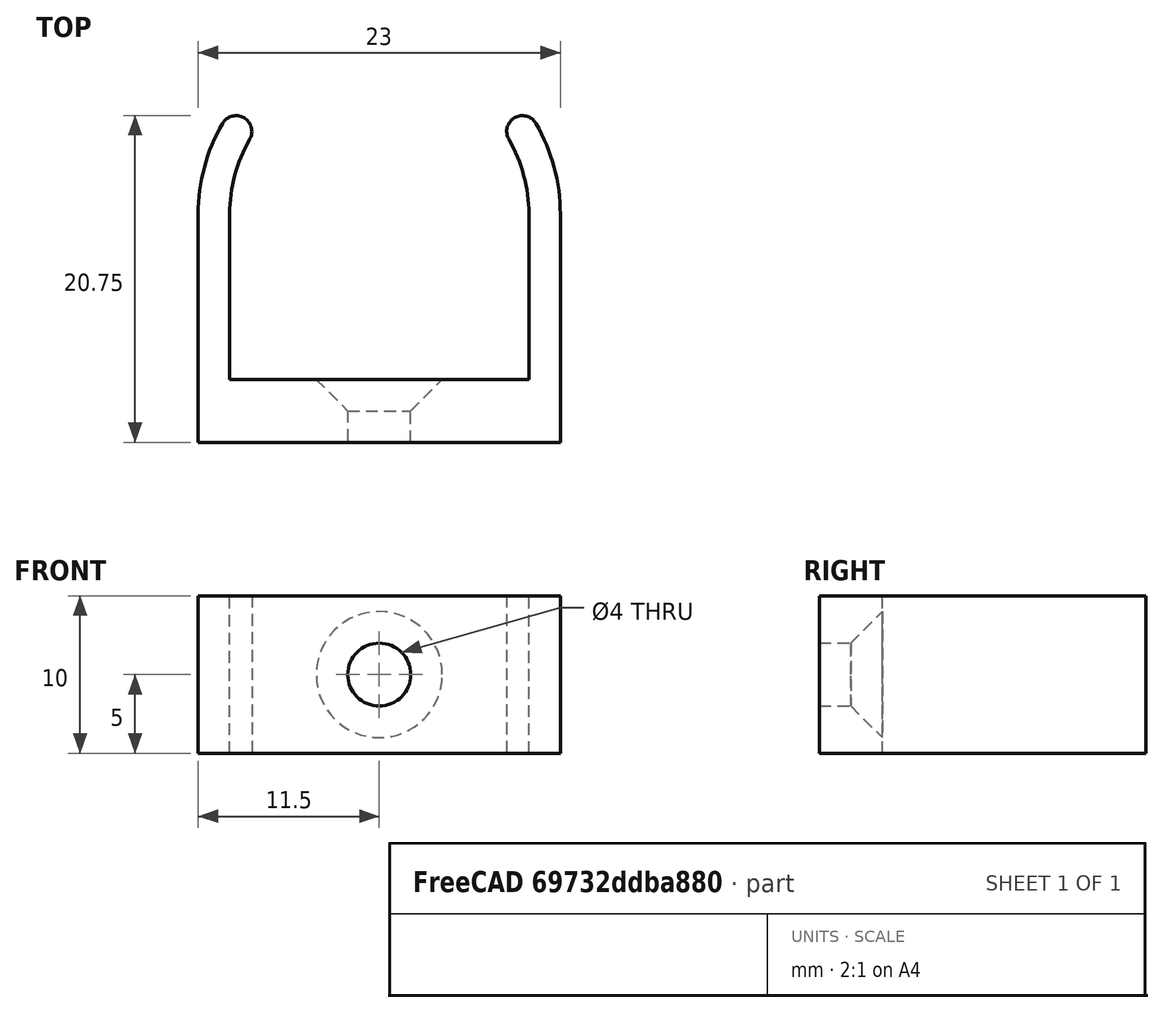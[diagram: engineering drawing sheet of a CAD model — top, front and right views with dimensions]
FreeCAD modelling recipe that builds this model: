
FCSTD DOCUMENT  (FreeCAD 0.20R)
Label: Support_batterie_V1
License: All rights reserved
LicenseURL: http://en.wikipedia.org/wiki/All_rights_reserved
objects: Sketcher::SketchObject×2, PartDesign::Pad×1, PartDesign::Pocket×1, PartDesign::Chamfer×1, PartDesign::Body×1, Mesh::Feature×1
note: 9 computed .brp shape members not serialized (recipe doc carries the construction recipe); baked Part::Feature solids carry a one-line shape summary decoded from their .brp

FEATURE [Sketcher::SketchObject] Sketch
  FullyConstrained = true
  MapMode = 5
  Support = -> [XY_Plane]
  sketch-geometry (15):
    g0: Circle CenterX=0 CenterY=0 CenterZ=0 NormalX=0 NormalY=0 NormalZ=1 AngleXU=0 Radius=9
    g1: ArcOfCircle CenterX=-1.4e-15 CenterY=0 CenterZ=0 NormalX=0 NormalY=0 NormalZ=1 AngleXU=0 Radius=11.5 StartAngle=2.61799 EndAngle=3.14159
    g2: ArcOfCircle CenterX=-1.4e-15 CenterY=0 CenterZ=0 NormalX=0 NormalY=0 NormalZ=1 AngleXU=0 Radius=11.5 StartAngle=0 EndAngle=0.523599
    g3: LineSegment StartX=-11.5 StartY=1.4e-15 StartZ=0 EndX=-11.5 EndY=-14.5 EndZ=0
    g4: LineSegment StartX=-11.5 StartY=-14.5 StartZ=0 EndX=11.5 EndY=-14.5 EndZ=0
    g5: LineSegment StartX=11.5 StartY=-14.5 StartZ=0 EndX=11.5 EndY=0 EndZ=0
    g6: LineSegment StartX=-9.95929 StartY=5.75 StartZ=0 EndX=-8.22724 EndY=4.75 EndZ=0
    g7: LineSegment StartX=8.22724 StartY=4.75 StartZ=0 EndX=9.95929 EndY=5.75 EndZ=0
    g8: ArcOfCircle CenterX=-9.09327 CenterY=5.25 CenterZ=0 NormalX=0 NormalY=0 NormalZ=1 AngleXU=0 Radius=1 StartAngle=5.75959 EndAngle=8.90118
    g9: ArcOfCircle CenterX=9.09327 CenterY=5.25 CenterZ=0 NormalX=0 NormalY=0 NormalZ=1 AngleXU=0 Radius=1 StartAngle=0.523599 EndAngle=3.66519
    g10: ArcOfCircle CenterX=0 CenterY=0 CenterZ=0 NormalX=0 NormalY=0 NormalZ=1 AngleXU=0 Radius=9.5 StartAngle=2.61799 EndAngle=3.14159
    g11: ArcOfCircle CenterX=0 CenterY=0 CenterZ=0 NormalX=0 NormalY=0 NormalZ=1 AngleXU=0 Radius=9.5 StartAngle=0 EndAngle=0.523599
    g12: LineSegment StartX=-9.5 StartY=1.2e-15 StartZ=0 EndX=-9.5 EndY=-10.5 EndZ=0
    g13: LineSegment StartX=-9.5 StartY=-10.5 StartZ=0 EndX=9.5 EndY=-10.5 EndZ=0
    g14: LineSegment StartX=9.5 StartY=-10.5 StartZ=0 EndX=9.5 EndY=0 EndZ=0
  constraints (41):
    c: Coincident(g0,g-1)
    c: Radius(g0) = 9
    c: Symmetric(g6,g7,g-2)
    c: Symmetric(g1,g2,g-2)
    c: Symmetric(g1,g2,g-2)
    c: Coincident(g3,g4)
    c: Horizontal(g4)
    c: Coincident(g4,g5)
    c: Coincident(g5,g2)
    c: Vertical(g3)
    c: Vertical(g5)
    c: Coincident(g6,g1)
    c: Coincident(g7,g2)
    c: PointOnObject(g8,g6)
    c: Coincident(g8,g1)
    c: PointOnObject(g9,g7)
    c: Coincident(g9,g2)
    c: Coincident(g1,g3)
    c: Coincident(g10,g-1)
    c: Coincident(g10,g8)
    c: PointOnObject(g10,g-1)
    c: Coincident(g11,g10)
    c: Coincident(g11,g9)
    c: PointOnObject(g11,g-1)
    c: Coincident(g2,g1)
    c: Coincident(g1,g10)
    c: Coincident(g6,g8)
    c: Perpendicular(g10,g6)
    c: Coincident(g7,g9)
    c: Tangent(g10,g12) = -1.5708
    c: Coincident(g12,g13)
    c: Horizontal(g13)
    c: Coincident(g13,g14)
    c: Coincident(g14,g11)
    c: Vertical(g14)
    c: DistanceY(g14,g14) = 10.5
    c: Distance(g6) = 2
    c: PointOnObject(g1,g-1)
    c: Radius(g10) = 9.5
    c: Distance(g12,g4) = 4
    c: Angle(g10) = 0.523599
FEATURE [PartDesign::Pad] Pad
  Direction = (0,0,1)
  Length = 10
  Length2 = 100
  Profile = -> Sketch
  Type = 0
FEATURE [Sketcher::SketchObject] Sketch001
  FullyConstrained = true
  MapMode = 5
  Placement = pos=(0,-10.5,0) rot=(0,0.707107,0.707107;3.14159rad)
  Support = -> [Pad]
  sketch-geometry (1):
    g0: Circle CenterX=0 CenterY=5 CenterZ=0 NormalX=0 NormalY=0 NormalZ=1 AngleXU=0 Radius=2
  constraints (3):
    c: PointOnObject(g0,g-2)
    c: Radius(g0) = 2
    c: DistanceY(g-1,g0) = 5
FEATURE [PartDesign::Pocket] Pocket
  BaseFeature = -> Pad
  Length = 8
  Length2 = 100
  Profile = -> Sketch001
  Type = 0
FEATURE [PartDesign::Chamfer] Chamfer
  Angle = 45
  Base = -> Pocket [Edge38]
  BaseFeature = -> Pocket
  ChamferType = 0
  FlipDirection = false
  Size = 2
  Size2 = 1
  SupportTransform = false
FEATURE [PartDesign::Body] Body
  Group = -> [Sketch,Pad,Sketch001,Pocket,Chamfer]
  Origin = -> Origin
  Tip = -> Chamfer
FEATURE [Mesh::Feature] Mesh  label="Body (Meshed)"
